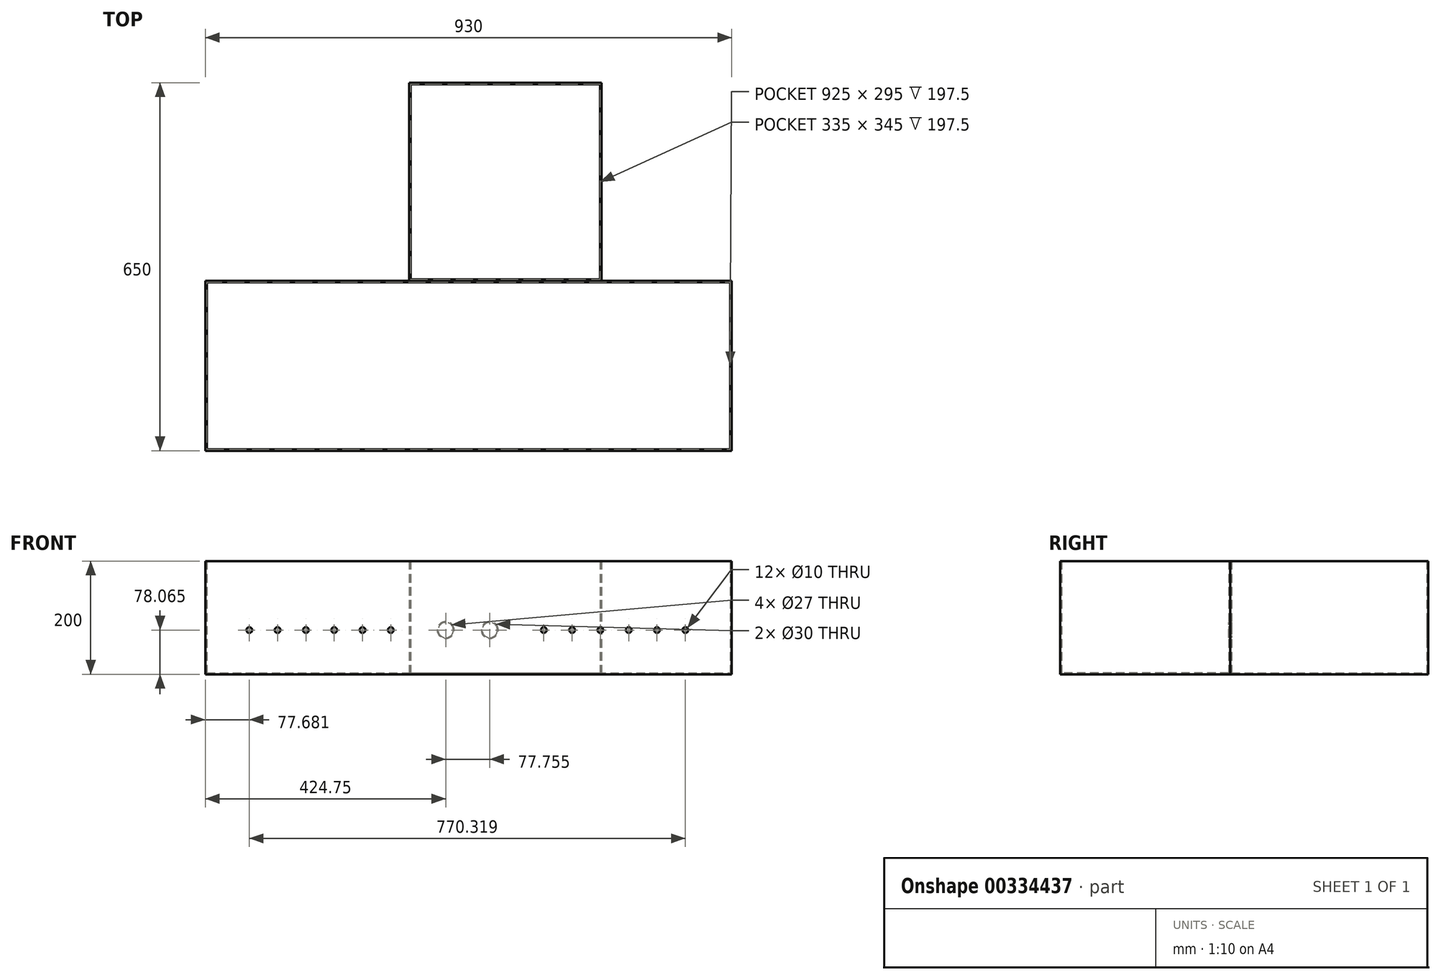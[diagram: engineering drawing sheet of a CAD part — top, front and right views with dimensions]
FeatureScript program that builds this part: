
annotation { "Feature Type Name" : "Feature", "Feature Type Description" : "" }
export const myFeature = defineFeature(function(context is Context, id is Id, definition is map)
    precondition{}
    {
        {
            var Q0;
            Q0=qCreatedBy(makeId("Top.planeOp"),FACE);
            var sketch = newSketch(context, id + "F0", { "sketchPlane" : qUnion([Q0])});
            skLineSegment(sketch, "E0.bottom", {"start": v(-465, 150) * mm, "end": v(465, 150) * mm});
            skLineSegment(sketch, "E0.top", {"start": v(-465, -150) * mm, "end": v(465, -150) * mm});
            skLineSegment(sketch, "E0.left", {"start": v(-465, 150) * mm, "end": v(-465, -150) * mm});
            skLineSegment(sketch, "E0.right", {"start": v(465, 150) * mm, "end": v(465, -150) * mm});
            skPoint(sketch, "E0.middle", {"position": v(0, 0) * mm});
            skSolve(sketch);
        }
        {
            var Q0;
            Q0=qCreatedBy(makeId("Top.planeOp"),FACE);
            var sketch = newSketch(context, id + "F1", { "sketchPlane" : qUnion([Q0])});
            skLineSegment(sketch, "E1.bottom", {"start": v(-105, 150) * mm, "end": v(235, 150) * mm});
            skLineSegment(sketch, "E1.top", {"start": v(-105, 500) * mm, "end": v(235, 500) * mm});
            skLineSegment(sketch, "E1.left", {"start": v(-105, 150) * mm, "end": v(-105, 500) * mm});
            skLineSegment(sketch, "E1.right", {"start": v(235, 150) * mm, "end": v(235, 500) * mm});
            skLineSegment(sketch, "E2", {"start": v(-105, 150) * mm, "end": v(-105, 32.22) * mm, "construction": true});
            skLineSegment(sketch, "E3", {"start": v(-105, 32.22) * mm, "end": v(-465, 32.22) * mm, "construction": true});
            skLineSegment(sketch, "E4", {"start": v(235, 150) * mm, "end": v(235, 22) * mm, "construction": true});
            skLineSegment(sketch, "E5", {"start": v(235, 22) * mm, "end": v(465, 22) * mm, "construction": true});
            skSolve(sketch);
        }
        {
            var Q0;
            Q0=makeQuery(id+"F0.imprint","IMPRINT",FACE,{"disambiguationData":[TD([[makeQuery(id+"F0.imprint","IMPRINT",EDGE,{"derivedFrom":sQuery(id+"F0.wireOp",EDGE,"E0.bottom")}),-1.0]])]});
            extrude(context, id + "F2", {"entities" : qUnion([Q0]), "depth" : 200 * mm});
        }
        {
            var Q0;
            Q0=makeQuery(id+"F2.opExtrude","CAP_FACE",FACE,{"disambiguationData":[OSD([sQuery(id+"F0.wireOp",EDGE,"E0.bottom"),sQuery(id+"F0.wireOp",EDGE,"E0.top"),sQuery(id+"F0.wireOp",EDGE,"E0.left"),sQuery(id+"F0.wireOp",EDGE,"E0.right")])],"isStart":false});
            shell(context, id + "F3", {"entities" : qUnion([Q0]), "thickness" : 2.5 * mm});
        }
        {
            var Q0;
            Q0=makeQuery(id+"F1.imprint","IMPRINT",FACE,{"disambiguationData":[TD([[makeQuery(id+"F1.imprint","IMPRINT",EDGE,{"derivedFrom":sQuery(id+"F1.wireOp",EDGE,"E1.bottom")}),1.0]])]});
            extrude(context, id + "F4", {"entities" : qUnion([Q0]), "depth" : 200 * mm});
        }
        {
            var Q0;
            Q0=makeQuery(id+"F4.opExtrude","CAP_FACE",FACE,{"disambiguationData":[OSD([sQuery(id+"F1.wireOp",EDGE,"E1.bottom"),sQuery(id+"F1.wireOp",EDGE,"E1.top"),sQuery(id+"F1.wireOp",EDGE,"E1.left"),sQuery(id+"F1.wireOp",EDGE,"E1.right")])],"isStart":false});
            shell(context, id + "F5", {"entities" : qUnion([Q0]), "thickness" : 2.5 * mm});
        }
        {
            var Q0;
            Q0=makeQuery(id+"F2.opExtrude","SWEPT_FACE",FACE,{"disambiguationData":[OSD([sQuery(id+"F0.wireOp",EDGE,"E0.top")])]});
            var sketch = newSketch(context, id + "F6", { "sketchPlane" : qUnion([Q0])});
            skLineSegment(sketch, "E6", {"start": v(-450, 200) * mm, "end": v(-450, 0) * mm, "construction": true});
            skLineSegment(sketch, "E7", {"start": v(450, 200) * mm, "end": v(450, 0) * mm, "construction": true});
            skLineSegment(sketch, "E8", {"start": v(450, 100) * mm, "end": v(465, 100) * mm, "construction": true});
            skLineSegment(sketch, "E9", {"start": v(-450, 100) * mm, "end": v(-465, 100) * mm, "construction": true});
            skLineSegment(sketch, "E10", {"start": v(-450, 100) * mm, "end": v(450, 100) * mm, "construction": true});
            skCircle(sketch, "E11", {"center": v(383, 78.06) * mm, "radius": 5 * mm});
            skLineSegment(sketch, "E12", {"start": v(383, 2.5) * mm, "end": v(383, 78.06) * mm, "construction": true});
            skLineSegment(sketch, "E13", {"start": v(450, 78.06) * mm, "end": v(383, 78.06) * mm, "construction": true});
            skCircle(sketch, "E14.1.0.0", {"center": v(333, 78.06) * mm, "radius": 5 * mm});
            skCircle(sketch, "E14.2.0.0", {"center": v(283, 78.06) * mm, "radius": 5 * mm});
            skCircle(sketch, "E14.3.0.0", {"center": v(233, 78.06) * mm, "radius": 5 * mm});
            skCircle(sketch, "E14.4.0.0", {"center": v(183, 78.06) * mm, "radius": 5 * mm});
            skCircle(sketch, "E14.5.0.0", {"center": v(133, 78.06) * mm, "radius": 5 * mm});
            skLineSegment(sketch, "E14.direction1", {"start": v(383, 78.06) * mm, "end": v(333, 78.06) * mm, "construction": true});
            skLineSegment(sketch, "E15", {"start": v(0, 0) * mm, "end": v(0, 200) * mm, "construction": true});
            skLineSegment(sketch, "E16", {"start": v(333, 78.06) * mm, "end": v(37.5, 78.06) * mm, "construction": true});
            skCircle(sketch, "E17", {"center": v(37.5, 78.06) * mm, "radius": 13.5 * mm});
            skLineSegment(sketch, "E18", {"start": v(37.5, 78.06) * mm, "end": v(37.5, 25.26) * mm, "construction": true});
            skLineSegment(sketch, "E19", {"start": v(37.5, 25.26) * mm, "end": v(450, 25.26) * mm, "construction": true});
            skCircle(sketch, "E20.MirrorC", {"center": v(-37.5, 78.06) * mm, "radius": 13.5 * mm});
            skCircle(sketch, "E21", {"center": v(-387.32, 78.06) * mm, "radius": 5 * mm});
            skLineSegment(sketch, "E22", {"start": v(-387.32, 78.06) * mm, "end": v(-450, 78.06) * mm, "construction": true});
            skCircle(sketch, "E23.1.0.0", {"center": v(-337.32, 78.06) * mm, "radius": 5 * mm});
            skCircle(sketch, "E23.2.0.0", {"center": v(-287.32, 78.06) * mm, "radius": 5 * mm});
            skCircle(sketch, "E23.3.0.0", {"center": v(-237.32, 78.06) * mm, "radius": 5 * mm});
            skCircle(sketch, "E23.4.0.0", {"center": v(-187.32, 78.06) * mm, "radius": 5 * mm});
            skCircle(sketch, "E23.5.0.0", {"center": v(-137.32, 78.06) * mm, "radius": 5 * mm});
            skLineSegment(sketch, "E23.direction1", {"start": v(-387.32, 78.06) * mm, "end": v(-337.32, 78.06) * mm, "construction": true});
            skSolve(sketch);
        }
        {
            var Q0;
            Q0=makeQuery(id+"F6.imprint","IMPRINT",FACE,{"disambiguationData":[TD([[makeQuery(id+"F6.imprint","IMPRINT",EDGE,{"derivedFrom":sQuery(id+"F6.wireOp",EDGE,"2fb40452-a07c-48d1-afae-638b5858da225.MirrorC")}),-1.0]])]});
            var Q1;
            Q1=makeQuery(id+"F6.imprint","IMPRINT",FACE,{"disambiguationData":[TD([[makeQuery(id+"F6.imprint","IMPRINT",EDGE,{"derivedFrom":sQuery(id+"F6.wireOp",EDGE,"2fb40452-a07c-48d1-afae-638b5858da224.MirrorC")}),-1.0]])]});
            var Q2;
            Q2=makeQuery(id+"F6.imprint","IMPRINT",FACE,{"disambiguationData":[TD([[makeQuery(id+"F6.imprint","IMPRINT",EDGE,{"derivedFrom":sQuery(id+"F6.wireOp",EDGE,"2fb40452-a07c-48d1-afae-638b5858da223.MirrorC")}),-1.0]])]});
            var Q3;
            Q3=makeQuery(id+"F6.imprint","IMPRINT",FACE,{"disambiguationData":[TD([[makeQuery(id+"F6.imprint","IMPRINT",EDGE,{"derivedFrom":sQuery(id+"F6.wireOp",EDGE,"2fb40452-a07c-48d1-afae-638b5858da222.MirrorC")}),-1.0]])]});
            var Q4;
            Q4=makeQuery(id+"F6.imprint","IMPRINT",FACE,{"disambiguationData":[TD([[makeQuery(id+"F6.imprint","IMPRINT",EDGE,{"derivedFrom":sQuery(id+"F6.wireOp",EDGE,"2fb40452-a07c-48d1-afae-638b5858da221.MirrorC")}),-1.0]])]});
            var Q5;
            Q5=makeQuery(id+"F6.imprint","IMPRINT",FACE,{"disambiguationData":[TD([[makeQuery(id+"F6.imprint","IMPRINT",EDGE,{"derivedFrom":sQuery(id+"F6.wireOp",EDGE,"2fb40452-a07c-48d1-afae-638b5858da220.MirrorC")}),-1.0]])]});
            var Q6;
            Q6=makeQuery(id+"F6.imprint","IMPRINT",FACE,{"disambiguationData":[TD([[makeQuery(id+"F6.imprint","IMPRINT",EDGE,{"derivedFrom":sQuery(id+"F6.wireOp",EDGE,"E14.5.0.0")}),1.0]])]});
            var Q7;
            Q7=makeQuery(id+"F6.imprint","IMPRINT",FACE,{"disambiguationData":[TD([[makeQuery(id+"F6.imprint","IMPRINT",EDGE,{"derivedFrom":sQuery(id+"F6.wireOp",EDGE,"E14.4.0.0")}),1.0]])]});
            var Q8;
            Q8=makeQuery(id+"F6.imprint","IMPRINT",FACE,{"disambiguationData":[TD([[makeQuery(id+"F6.imprint","IMPRINT",EDGE,{"derivedFrom":sQuery(id+"F6.wireOp",EDGE,"E14.3.0.0")}),1.0]])]});
            var Q9;
            Q9=makeQuery(id+"F6.imprint","IMPRINT",FACE,{"disambiguationData":[TD([[makeQuery(id+"F6.imprint","IMPRINT",EDGE,{"derivedFrom":sQuery(id+"F6.wireOp",EDGE,"E14.2.0.0")}),1.0]])]});
            var Q10;
            Q10=makeQuery(id+"F6.imprint","IMPRINT",FACE,{"disambiguationData":[TD([[makeQuery(id+"F6.imprint","IMPRINT",EDGE,{"derivedFrom":sQuery(id+"F6.wireOp",EDGE,"E11")}),1.0]])]});
            var Q11;
            Q11=makeQuery(id+"F6.imprint","IMPRINT",FACE,{"disambiguationData":[TD([[makeQuery(id+"F6.imprint","IMPRINT",EDGE,{"derivedFrom":sQuery(id+"F6.wireOp",EDGE,"E14.1.0.0")}),1.0]])]});
            var Q12;
            Q12=makeQuery(id+"F6.imprint","IMPRINT",FACE,{"disambiguationData":[TD([[makeQuery(id+"F6.imprint","IMPRINT",EDGE,{"derivedFrom":sQuery(id+"F6.wireOp",EDGE,"E23.5.0.0")}),1.0]])]});
            var Q13;
            Q13=makeQuery(id+"F6.imprint","IMPRINT",FACE,{"disambiguationData":[TD([[makeQuery(id+"F6.imprint","IMPRINT",EDGE,{"derivedFrom":sQuery(id+"F6.wireOp",EDGE,"E23.4.0.0")}),1.0]])]});
            var Q14;
            Q14=makeQuery(id+"F6.imprint","IMPRINT",FACE,{"disambiguationData":[TD([[makeQuery(id+"F6.imprint","IMPRINT",EDGE,{"derivedFrom":sQuery(id+"F6.wireOp",EDGE,"E23.3.0.0")}),1.0]])]});
            var Q15;
            Q15=makeQuery(id+"F6.imprint","IMPRINT",FACE,{"disambiguationData":[TD([[makeQuery(id+"F6.imprint","IMPRINT",EDGE,{"derivedFrom":sQuery(id+"F6.wireOp",EDGE,"E23.2.0.0")}),1.0]])]});
            var Q16;
            Q16=makeQuery(id+"F6.imprint","IMPRINT",FACE,{"disambiguationData":[TD([[makeQuery(id+"F6.imprint","IMPRINT",EDGE,{"derivedFrom":sQuery(id+"F6.wireOp",EDGE,"E23.1.0.0")}),1.0]])]});
            var Q17;
            Q17=makeQuery(id+"F6.imprint","IMPRINT",FACE,{"disambiguationData":[TD([[makeQuery(id+"F6.imprint","IMPRINT",EDGE,{"derivedFrom":sQuery(id+"F6.wireOp",EDGE,"E21")}),1.0]])]});
            extrude(context, id + "F7", {"entities" : qUnion([Q0, Q1, Q2, Q3, Q4, Q5, Q6, Q7, Q8, Q9, Q10, Q11, Q12, Q13, Q14, Q15, Q16, Q17]), "operationType" : NewBodyOperationType.REMOVE, "oppositeDirection" : true, "depth" : 25 * mm});
        }
        {
            var Q0;
            Q0=makeQuery(id+"F3.opShell","OFFSET_FACE",FACE,{"disambiguationData":[OSD([sQuery(id+"F0.wireOp",EDGE,"E0.bottom")])]});
            var sketch = newSketch(context, id + "F8", { "sketchPlane" : qUnion([Q0])});
            skCircle(sketch, "E24", {"center": v(37.5, 78.06) * mm, "radius": 13.5 * mm});
            skCircle(sketch, "E25", {"center": v(-40.25, 78.06) * mm, "radius": 13.5 * mm});
            skLineSegment(sketch, "E26", {"start": v(37.5, 78.06) * mm, "end": v(-40.25, 78.06) * mm, "construction": true});
            skSolve(sketch);
        }
        {
            var Q0;
            Q0 = qSketchRegion(id + "F8", true);
            extrude(context, id + "F9", {"entities" : qUnion([Q0]), "operationType" : NewBodyOperationType.REMOVE, "oppositeDirection" : true, "depth" : 25 * mm});
        }
        {
            var Q0;
            Q0=makeQuery(id+"F4.opExtrude","SWEPT_FACE",FACE,{"disambiguationData":[OSD([sQuery(id+"F1.wireOp",EDGE,"E1.top")])]});
            var sketch = newSketch(context, id + "F10", { "sketchPlane" : qUnion([Q0])});
            skCircle(sketch, "E27", {"center": v(-37.5, 78.06) * mm, "radius": 15 * mm});
            skCircle(sketch, "E28", {"center": v(40.25, 78.06) * mm, "radius": 15 * mm});
            skSolve(sketch);
        }
        {
            var Q0;
            Q0 = qSketchRegion(id + "F10", true);
            extrude(context, id + "F11", {"entities" : qUnion([Q0]), "operationType" : NewBodyOperationType.REMOVE, "oppositeDirection" : true, "depth" : 25 * mm});
        }
    });
